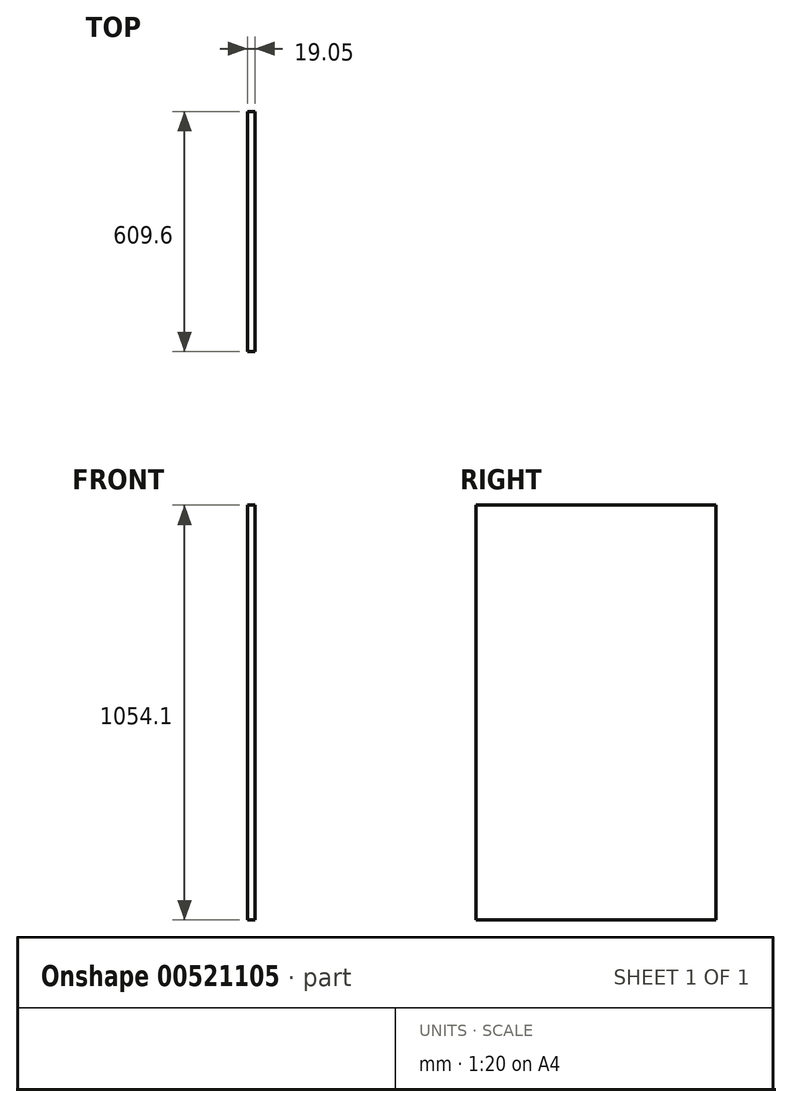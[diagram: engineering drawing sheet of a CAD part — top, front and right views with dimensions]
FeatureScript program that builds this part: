
annotation { "Feature Type Name" : "Feature", "Feature Type Description" : "" }
export const myFeature = defineFeature(function(context is Context, id is Id, definition is map)
    precondition{}
    {
        {
            var Q0;
            Q0=qCreatedBy(makeId("Right.planeOp"),FACE);
            var sketch = newSketch(context, id + "F0", { "sketchPlane" : qUnion([Q0])});
            skLineSegment(sketch, "E0.bottom", {"start": v(-304.8, 527.05) * mm, "end": v(304.8, 527.05) * mm});
            skLineSegment(sketch, "E0.top", {"start": v(-304.8, -527.05) * mm, "end": v(304.8, -527.05) * mm});
            skLineSegment(sketch, "E0.left", {"start": v(-304.8, 527.05) * mm, "end": v(-304.8, -527.05) * mm});
            skLineSegment(sketch, "E0.right", {"start": v(304.8, 527.05) * mm, "end": v(304.8, -527.05) * mm});
            skPoint(sketch, "E0.middle", {"position": v(0, 0) * mm});
            skSolve(sketch);
        }
        {
            var Q0;
            Q0=makeQuery(id+"F0.imprint","IMPRINT",FACE,{"disambiguationData":[TD([[makeQuery(id+"F0.imprint","IMPRINT",EDGE,{"derivedFrom":sQuery(id+"F0.wireOp",EDGE,"E0.bottom")}),-1.0]])]});
            extrude(context, id + "F1", {"entities" : qUnion([Q0]), "depth" : 19.05 * mm, "offsetDistance" : 25.4 * mm});
        }
    });
